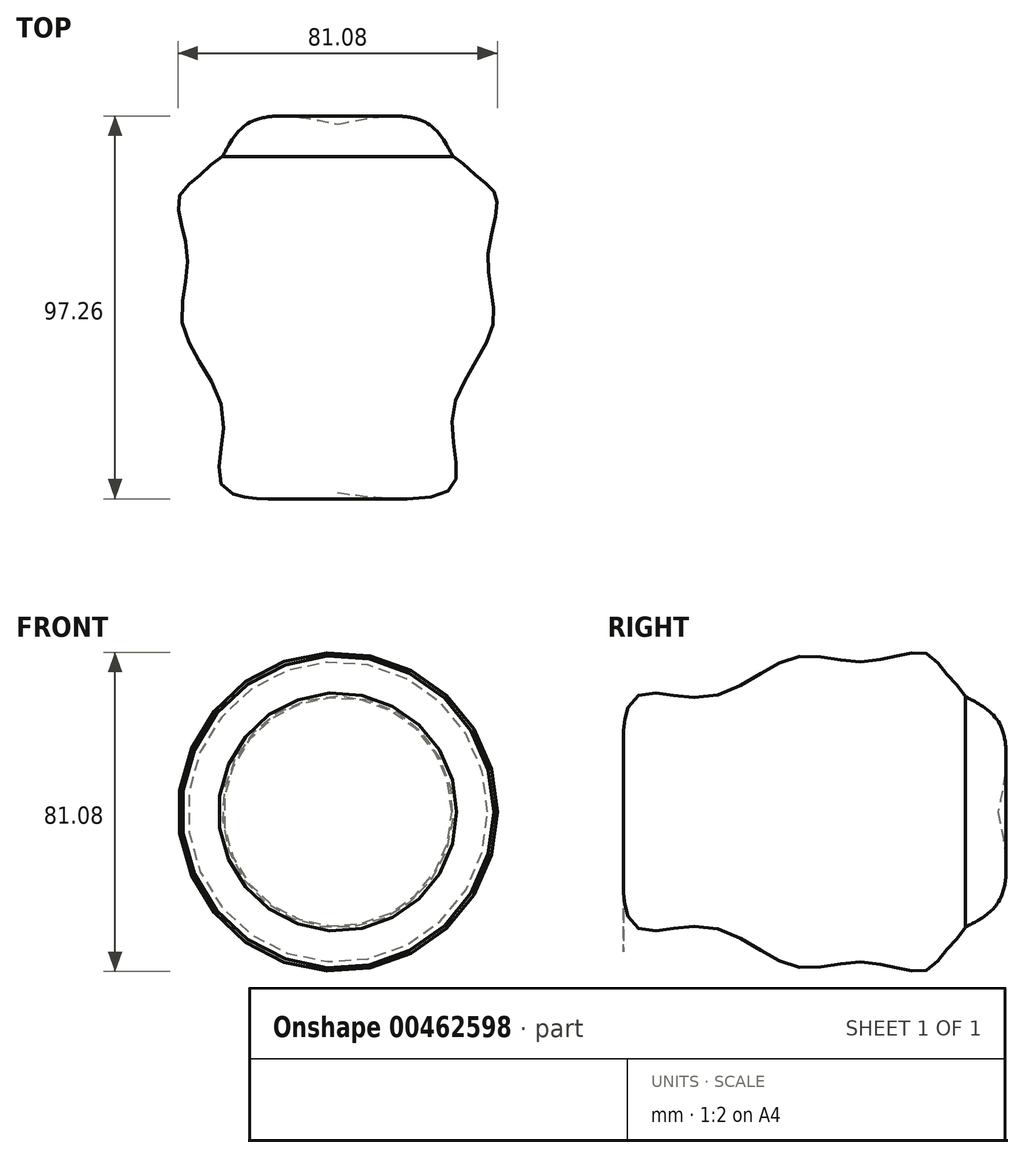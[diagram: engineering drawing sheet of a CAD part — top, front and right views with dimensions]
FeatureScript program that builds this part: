
annotation { "Feature Type Name" : "Feature", "Feature Type Description" : "" }
export const myFeature = defineFeature(function(context is Context, id is Id, definition is map)
    precondition{}
    {
        {
            var Q0;
            Q0=qCreatedBy(makeId("Top.planeOp"),FACE);
            var sketch = newSketch(context, id + "F0", { "sketchPlane" : qUnion([Q0])});
            skFitSpline(sketch, "E0", {"points": [v(-7, -43.45) * mm, v(29.16, -42.88) * mm, v(29.16, -24.37) * mm, v(39.28, -2.39) * mm, v(38.12, 14.68) * mm, v(40.44, 30.3) * mm, v(35.52, 35.8) * mm, v(28.58, 41) * mm, v(28.87, 25.1) * mm, v(29.74, 11.79) * mm, v(30.32, -3.25) * mm, v(21.06, -22.63) * mm, v(23.08, -37.67) * mm, v(-9.3, -37.1) * mm], "startDerivative": vector(412.9, -58.45) * mm, "endDerivative": vector(-433.28, 61.9) * mm});
            skLineSegment(sketch, "E1", {"start": v(0, 52.86) * mm, "end": v(0, -57.92) * mm});
            skFitSpline(sketch, "E2", {"points": [v(-3.23, 48.52) * mm, v(23.66, 48.8) * mm, v(29.4, 41) * mm, v(28.58, 48.23) * mm], "startDerivative": vector(67.05, 14.92) * mm, "endDerivative": vector(-7.42, 44.72) * mm});
            skFitSpline(sketch, "E3", {"points": [v(21.06, 49.67) * mm, v(21.06, 50.54) * mm], "startDerivative": vector(0, 0.87) * mm, "endDerivative": vector(0, 0.87) * mm});
            skSolve(sketch);
        }
        {
            var Q0;
            Q0 = qSketchRegion(id + "F0", true);
            var Q1;
            Q1=sQuery(id+"F0.wireOp",EDGE,"E1");
            revolve(context, id + "F1", {"entities" : qUnion([Q0]), "axis" : qUnion([Q1]), "revolveType" : RevolveType.FULL});
        }
    });
